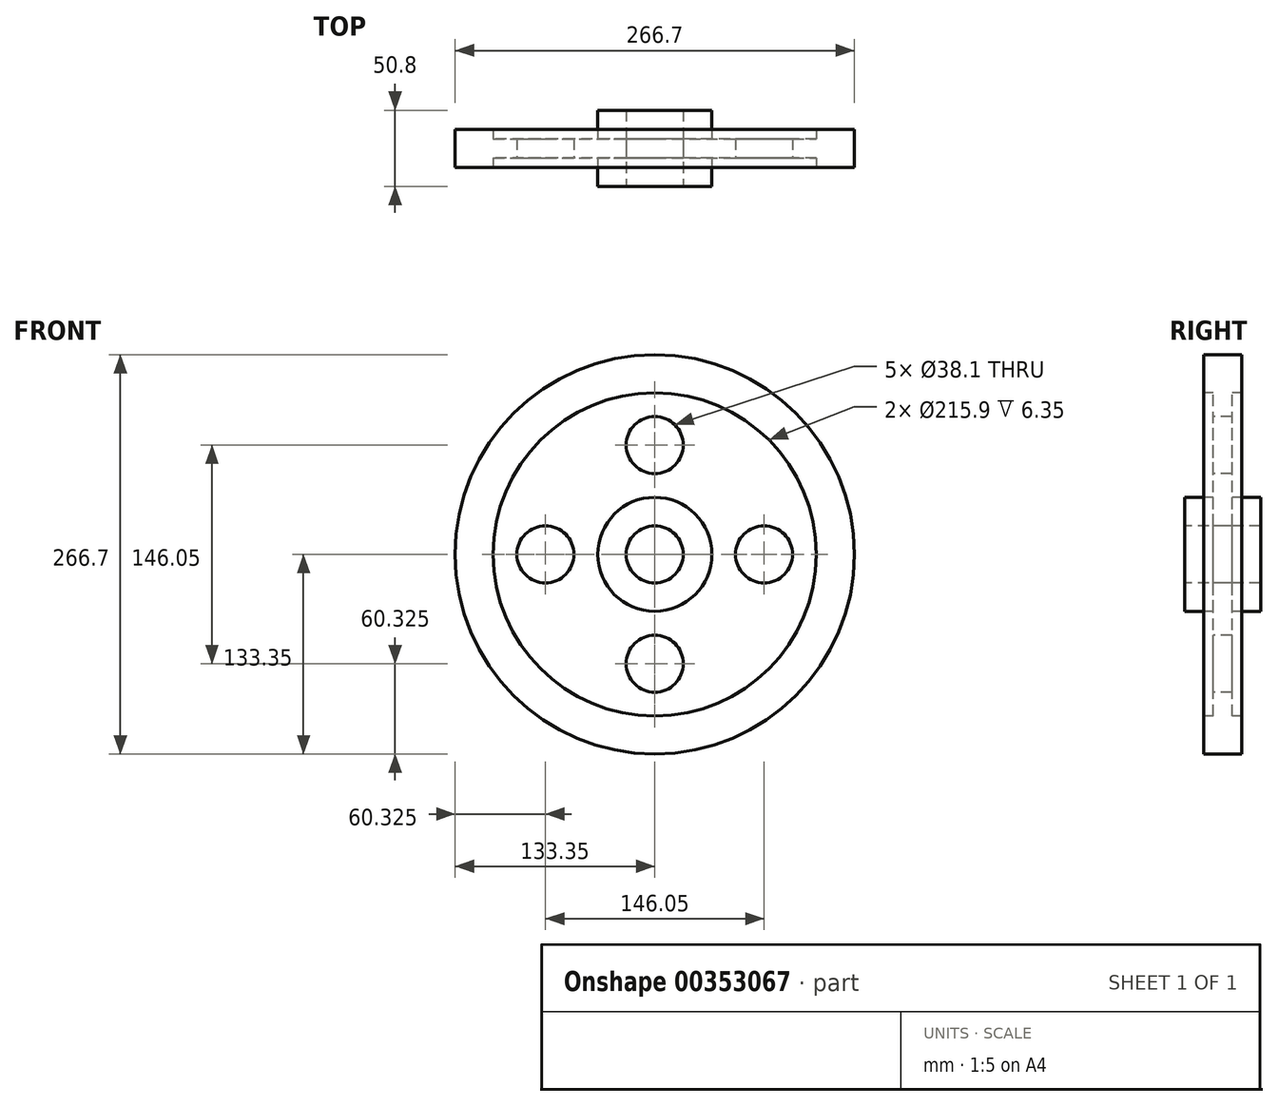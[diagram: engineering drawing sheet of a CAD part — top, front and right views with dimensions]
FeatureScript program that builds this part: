
annotation { "Feature Type Name" : "Feature", "Feature Type Description" : "" }
export const myFeature = defineFeature(function(context is Context, id is Id, definition is map)
    precondition{}
    {
        {
            var Q0;
            Q0=qCreatedBy(makeId("Right.planeOp"),FACE);
            var sketch = newSketch(context, id + "F0", { "sketchPlane" : qUnion([Q0])});
            skLineSegment(sketch, "E0", {"start": v(0, 0) * mm, "end": v(76.96, 0) * mm, "construction": true});
            skLineSegment(sketch, "E1.0", {"start": v(0, 19.05) * mm, "end": v(25.4, 19.05) * mm, "construction": true});
            skLineSegment(sketch, "E2.0", {"start": v(6.35, 38.1) * mm, "end": v(25.4, 38.1) * mm});
            skLineSegment(sketch, "E3.0", {"start": v(6.35, 107.95) * mm, "end": v(12.7, 107.95) * mm});
            skLineSegment(sketch, "E4.0", {"start": v(0, 133.35) * mm, "end": v(12.7, 133.35) * mm});
            skLineSegment(sketch, "E5", {"start": v(0, 0) * mm, "end": v(-76.8, 0) * mm, "construction": true});
            skLineSegment(sketch, "E6", {"start": v(0, 0) * mm, "end": v(0, 133.35) * mm, "construction": true});
            skLineSegment(sketch, "E7.0", {"start": v(25.4, 19.05) * mm, "end": v(25.4, 38.1) * mm});
            skLineSegment(sketch, "E8.trimOffspring", {"start": v(12.7, 107.95) * mm, "end": v(12.7, 133.35) * mm});
            skLineSegment(sketch, "E9.trimOffspring", {"start": v(6.35, 38.1) * mm, "end": v(6.35, 107.95) * mm});
            skLineSegment(sketch, "E10", {"start": v(0, 19.05) * mm, "end": v(25.4, 19.05) * mm});
            skLineSegment(sketch, "E11.MirrorCS", {"start": v(0, 133.35) * mm, "end": v(-12.7, 133.35) * mm});
            skLineSegment(sketch, "E12.MirrorCS", {"start": v(-12.7, 107.95) * mm, "end": v(-12.7, 133.35) * mm});
            skLineSegment(sketch, "E13.MirrorCS", {"start": v(-6.35, 38.1) * mm, "end": v(-6.35, 107.95) * mm});
            skLineSegment(sketch, "E14.MirrorCS", {"start": v(-6.35, 38.1) * mm, "end": v(-25.4, 38.1) * mm});
            skLineSegment(sketch, "E15.MirrorCS", {"start": v(-25.4, 19.05) * mm, "end": v(-25.4, 38.1) * mm});
            skLineSegment(sketch, "E16.MirrorCS", {"start": v(0, 19.05) * mm, "end": v(-25.4, 19.05) * mm});
            skLineSegment(sketch, "E17", {"start": v(-12.7, 107.95) * mm, "end": v(-6.35, 107.95) * mm});
            skSolve(sketch);
        }
        {
            var Q0;
            Q0=makeQuery(id+"F0.imprint","IMPRINT",FACE,{"disambiguationData":[TD([[makeQuery(id+"F0.imprint","IMPRINT",EDGE,{"derivedFrom":sQuery(id+"F0.wireOp",EDGE,"E2.0")}),-1.0]])]});
            var Q1;
            Q1=sQuery(id+"F0.wireOp",EDGE,"E0");
            revolve(context, id + "F1", {"entities" : qUnion([Q0]), "axis" : qUnion([Q1]), "revolveType" : RevolveType.FULL});
        }
        {
            var Q0;
            Q0=makeQuery(id+"F1.opRevolve","SWEPT_FACE",FACE,{"disambiguationData":[OSD([sQuery(id+"F0.wireOp",EDGE,"E13.MirrorCS")])]});
            var sketch = newSketch(context, id + "F2", { "sketchPlane" : qUnion([Q0])});
            skLineSegment(sketch, "E18", {"start": v(0, 0) * mm, "end": v(0, 73.02) * mm});
            skCircle(sketch, "E19", {"center": v(0, 73.02) * mm, "radius": 19.05 * mm});
            skCircle(sketch, "E20.1.0", {"center": v(-73.02, 0) * mm, "radius": 19.05 * mm});
            skCircle(sketch, "E20.2.0", {"center": v(0, -73.02) * mm, "radius": 19.05 * mm});
            skCircle(sketch, "E20.3.0", {"center": v(73.02, 0) * mm, "radius": 19.05 * mm});
            skPoint(sketch, "E20.center", {"position": v(0, 0) * mm});
            skSolve(sketch);
        }
        {
            var Q0;
            Q0=makeQuery(id+"F2.imprint","IMPRINT",FACE,{"disambiguationData":[TD([[makeQuery(id+"F2.imprint","IMPRINT",EDGE,{"derivedFrom":sQuery(id+"F2.wireOp",EDGE,"E19")}),1.0]])]});
            var Q1;
            Q1=makeQuery(id+"F2.imprint","IMPRINT",FACE,{"disambiguationData":[TD([[makeQuery(id+"F2.imprint","IMPRINT",EDGE,{"derivedFrom":sQuery(id+"F2.wireOp",EDGE,"E20.1.0")}),1.0]])]});
            var Q2;
            Q2=makeQuery(id+"F2.imprint","IMPRINT",FACE,{"disambiguationData":[TD([[makeQuery(id+"F2.imprint","IMPRINT",EDGE,{"derivedFrom":sQuery(id+"F2.wireOp",EDGE,"E20.2.0")}),1.0]])]});
            var Q3;
            Q3=makeQuery(id+"F2.imprint","IMPRINT",FACE,{"disambiguationData":[TD([[makeQuery(id+"F2.imprint","IMPRINT",EDGE,{"derivedFrom":sQuery(id+"F2.wireOp",EDGE,"E20.3.0")}),1.0]])]});
            extrude(context, id + "F3", {"entities" : qUnion([Q0, Q1, Q2, Q3]), "operationType" : NewBodyOperationType.REMOVE, "oppositeDirection" : true, "depth" : 25.4 * mm});
        }
    });
